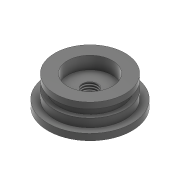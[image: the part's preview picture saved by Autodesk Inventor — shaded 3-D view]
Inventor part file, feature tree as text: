
AUTODESK INVENTOR PART (.ipt)
format: ipt  version: 2022.3 (Build 263350000, 350)  size: 141,312 bytes
history: native  units: mm
features: extrude x6, sketch x6, other x1, thread x1, plane x1
ambient origin geometry x8: Origin, YZ Plane, XZ Plane, XY Plane, X Axis, Y Axis, Z Axis, Center Point
bodies: Body1 (feature_tree)
feature tree (15):
  other  "Sólido1"
  extrude  "Extrusión1"  Depth=4.0mm TaperAngle=0.0deg
  extrude  "Extrusión2"  Depth=13.8mm TaperAngle=0.0deg
  extrude  "Extrusión3"  Depth=7.85mm TaperAngle=0.0deg
  extrude  "Extrusión4"  Depth=12.0mm TaperAngle=0.0deg
  extrude  "Extrusión5"  Depth=3.0mm TaperAngle=0.0deg
  thread  "Rosca1"  [1 undecoded]
  plane  "Plano de trabajo1"
  extrude  "Extrusión6"  Depth=5.0mm
  sketch  "Boceto1"  dims[d0=52.0mm d1=4.0mm d2=0.0mm]
  sketch  "Boceto2"  dims[d3=43.55mm d4=13.8mm d5=0.0mm]
  sketch  "Boceto3"  dims[d6=27.75mm d7=7.85mm d8=0.0mm]
  sketch  "Boceto4"  dims[d9=9.6mm d10=12.0mm d11=0.0mm]
  sketch  "Boceto5"  dims[d12=42.4mm d13=3.0mm d14=0.0mm d15=6.95mm d16=0.0mm]
  sketch  "Boceto6"  dims[d17=-3.6mm d18=37.85mm d19=5.0mm d20=0.0mm]
note: 1 required parameter value undecoded (feature->parameter linkage not recoverable at this tier; creation-order binding heuristic only, values carry confidence <= 0.55)
